# Revit family: PRD_FrankeWS_JntrlUnits_SiriusMultiPurposeSink_BS332,BS333
name_source: partatom
category: Plumbing Fixtures
revit_build: Autodesk Revit 2018 (Build: 20190510_1515(x64)
units: mm (PartAtom-declared; Revit-internal decimal feet)

## family parameters
Cut with Voids When Loaded = No
Host = Face
OmniClass Number = 23.45.05.14.14
OmniClass Title = Sinks/Lavatories
Part Type = Normal
Room Calculation Point = No
Round Connector Dimension = Use Diameter
Shared = No

## types (2) — shared parameters
AssetType = Fixed
Category = Pr_40_20_96_44, Janitorial sinks
Color = Stainless steel
Default Elevation = 850 mm  [stored 2.78871 ft]
DrainSize = DN-40-1-1-2INH
DurationUnit = year
Features = stainless steel, 1.00 mm, satin finished, wall mounting, 1000x270x500 mm (WxHxD)
Finish = Satin finished
FinishAndMaterial = Stainless steel 1.4301
Form = Stainless steel multi purpose sink
IfcExportAs = IfcSanitaryTerminalType
IfcExportType = SINK
Manufacturer = KWC Group AG
ManufacturerName = KWC Group AG
ManufacturerURL = www.kwc.com
Material = Stainless steel
NBSDescription = Janitorial units
NBSReference = 45-35-70/401
NominalDepth = 500 mm  [stored 1.64042 ft]
NominalHeight = 270 mm  [stored 0.885827 ft]
NominalWidth = 1000 mm  [stored 3.28084 ft]
ProductInformation = https://pim.kwc.com
Shape = Rectangular
SinkMaterial = PRD_AR_StainlessSteel_SatinFinished
SinkMounting = WallHung
SinkType = Other
Size = 1000 x 500 x 270 mm
URL = www.kwc.com
Uniclass2015Code = Pr_40_20_96_44
Uniclass2015Title = Janitorial sinks
Uniclass2015Version = Products v1.5
Version = 1
WarrantyDurationUnit = year
WasteSize = 1 1/2"
WaterSupplyOverflowAndWasteHolesOverflow = Stand pipe overflow
WaterSupplyOverflowAndWasteHolesWaste = Center-Back
WaterSupplyOverflowAndWasteHolesWaterSupply = No tapholes
zero-valued in all types: NominalLength

## per-type parameters (varying)
| type | BIMObjectName | Description | GrossWeight | Left | ModelNumber | Name | NetWeight | Right |
| BS332 | PRD_AR_JanitorialUnits_SiriusMultiPurposeSink_BS332 | Wall mounted general purpose sink top, stainless steel, surface satin finished, flat drainer / work area, tap ledge 70 mm, 38 mm waste fitting with 1 1/2'' standing plug/overflow tube, complete with integral wall brackets, screws and dowels. Storage board left. | 12.24 kg | Yes | 2000100077 | Sirius multi purpose sink BS332 | 10.16 kg | No |
| BS333 | PRD_AR_JanitorialUnits_SiriusMultiPurposeSink_BS333 | Wall mounted general purpose sink top, stainless steel, surface satin finished, flat drainer / work area, tap ledge 70 mm, 38 mm waste fitting with 1 1/2'' standing plug/overflow tube, complete with integral wall brackets, screws and dowels. Storage board right. | 12.90 kg | No | 2000100078 | Sirius multi purpose sink BS333 | 12.11 kg | Yes |

note: column(s) folded — value = type name in every type: Model, ModelReference

note: [stored X ft] marks values corroborated as IEEE doubles in the binary element streams (Revit-internal decimal feet)

## geometry (parser evidence)
native form markers: Sweep x3
no freeform markers — native parametric forms only
